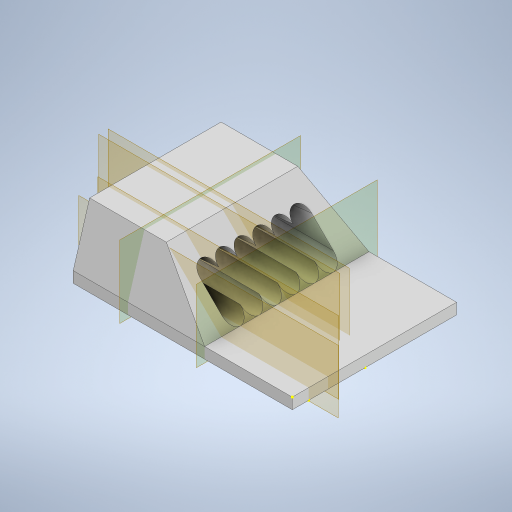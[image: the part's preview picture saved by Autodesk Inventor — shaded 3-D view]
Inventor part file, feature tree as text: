
AUTODESK INVENTOR PART (.ipt)
format: ipt  version: 2023 (Build 270158000, 158)  size: 418,304 bytes
history: native  units: mm
features: sketch x11, plane x6, extrude x5, loft x1
ambient origin geometry x8: Origin, YZ Plane, XZ Plane, XY Plane, X Axis, Y Axis, Z Axis, Center Point
bodies: 实体1 (feature_tree)
feature tree (23):
  extrude  "拉伸1"  Depth=15.0mm
  sketch  "草图2"  dims[d3=1.0mm d4=0.0mm d5=-1.5mm]
  plane  "工作平面1"
  extrude  "拉伸2"  [1 undecoded]
  extrude  "拉伸3"  Depth=12.0mm
  plane  "工作平面3"
  sketch  "草图6"  dims[d13=12.0mm d14=0.0mm d39=0.85mm]
  extrude  "拉伸5"  Depth=12.0mm TaperAngle=0.0deg
  sketch  "草图8"  dims[d44=-5.0mm]
  plane  "工作平面4"
  sketch  "草图9"  dims[d54=1.7mm]
  plane  "工作平面5"
  sketch  "草图10"  dims[d55=3.2mm]
  plane  "工作平面6"
  loft  "放样1"
  extrude  "拉伸6"  TaperAngle=0.0deg  [1 undecoded]
  sketch  "草图1"  dims[d1=15.0mm d2=20.0mm]
  sketch  "草图3"  dims[d6=5.0mm d8=12.0mm]
  sketch  "草图4"  dims[d10=0.0mm d11=12.0mm d12=0.0mm]
  plane  "工作平面2"
  sketch  "草图7"  dims[d41=45.0deg d42=0.0mm d43=0.0mm]
  sketch  "草图11"  dims[d56=60.0mm d58=1.7mm d59=10.0mm d61=10.0mm]
  sketch  "草图12"  dims[d63=7.5mm d64=1.7mm d65=4.0mm d66=60.0mm d68=1.7mm d69=10.0mm d71=10.0mm d73=7.5mm d74=4.0mm d75=3.2mm d76=7.0mm d77=0.0mm d78=90.0deg d79=0.0mm d80=90.0deg d81=0.0mm d82=90.0deg d83=0.0mm d84=90.0deg d85=60.0mm d87=1.7mm d88=10.0mm d90=10.0mm d92=0.0mm d93=0.0mm]
note: 2 required parameter values undecoded (feature->parameter linkage not recoverable at this tier; creation-order binding heuristic only, values carry confidence <= 0.55)
